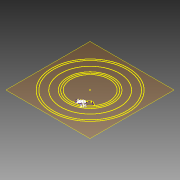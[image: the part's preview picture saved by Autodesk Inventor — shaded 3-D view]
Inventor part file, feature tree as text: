
AUTODESK INVENTOR PART (.ipt)
format: ipt  version: 2015 SP1 (Build 190203100, 203)  size: 407,040 bytes
history: native  units: in
note: dims shown in document units (in); Inventor stores cm internally (conversion verified against a paired STEP export)
features: other x5, plane x1, projected_geometry x1
ambient origin geometry x8: Origin, YZ Plane, XZ Plane, XY Plane, X Axis, Y Axis, Z Axis, Center Point
bodies: Solid1 (feature_tree)
feature tree (7):
  other  "Wheel Blank Pro 83mm.ipt"
  plane  "Work Plane1"
  other  "Spokes"
  other  "Circles"
  other  "Solid1::Wheel Blank Pro 83mm.ipt"
  other  "TaggingFeature1"
  projected_geometry  "Projected Loop26"
